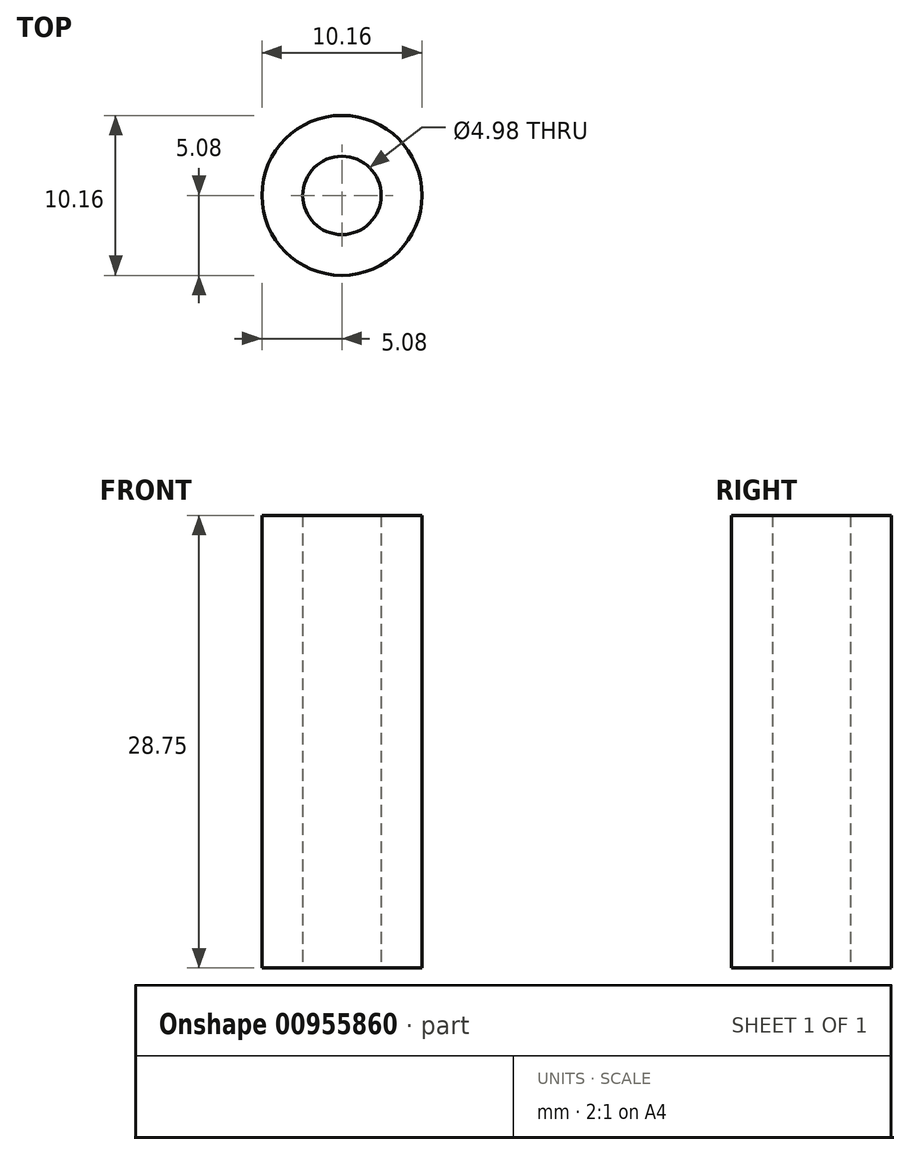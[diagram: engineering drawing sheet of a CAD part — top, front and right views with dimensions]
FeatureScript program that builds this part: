
annotation { "Feature Type Name" : "Feature", "Feature Type Description" : "" }
export const myFeature = defineFeature(function(context is Context, id is Id, definition is map)
    precondition{}
    {
        {
            var Q0;
            Q0=qCreatedBy(makeId("Top.planeOp"),FACE);
            var sketch = newSketch(context, id + "F0", { "sketchPlane" : qUnion([Q0])});
            skCircle(sketch, "E0", {"center": v(0, 0) * mm, "radius": 2.49 * mm});
            skCircle(sketch, "E1", {"center": v(0, 0) * mm, "radius": 5.08 * mm});
            skSolve(sketch);
        }
        {
            var Q0;
            Q0=makeQuery(id+"F0.imprint","IMPRINT",FACE,{"disambiguationData":[TD([[makeQuery(id+"F0.imprint","IMPRINT",EDGE,{"derivedFrom":sQuery(id+"F0.wireOp",EDGE,"E0")}),-1.0]])]});
            extrude(context, id + "F1", {"entities" : qUnion([Q0]), "depth" : 28.75 * mm, "offsetDistance" : 25.4 * mm});
        }
    });
